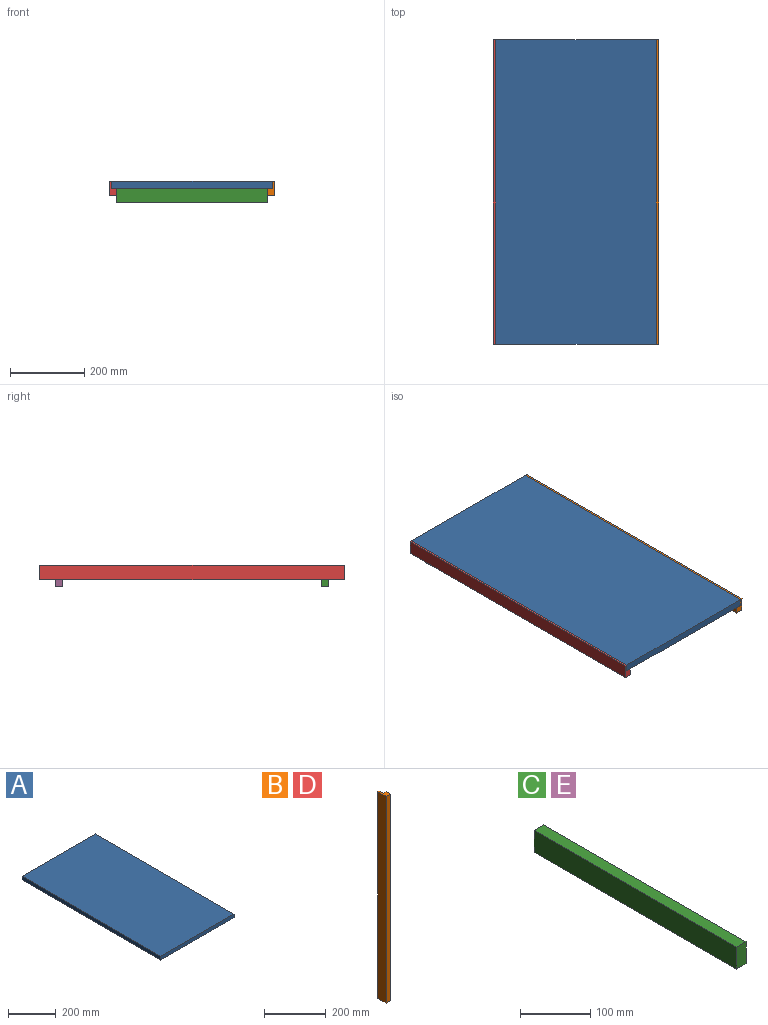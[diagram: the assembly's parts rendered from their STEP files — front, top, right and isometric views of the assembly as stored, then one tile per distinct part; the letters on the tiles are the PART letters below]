
ASSEMBLY  parts=5 mates=4
PART A: 6 faces, bbox 431.8x819.2x19.1 mm
  f0: plane 819.15x19.05mm, normal (-1,0,0), area 15604.8mm2, adj f1,f2,f3,f4
  f1: plane 819.15x431.8mm, normal (0,0,-1), area 353709mm2, adj f0,f2,f4,f5
  f2: plane 431.8x19.05mm, normal (0,1,0), area 8225.8mm2, adj f0,f1,f3,f5
  f3: plane 819.15x431.8mm, normal (0,0,1), area 353709mm2, adj f0,f2,f4,f5
  f4: plane 431.8x19.05mm, normal (0,-1,0), area 8225.8mm2, adj f0,f1,f3,f5
  f5: plane 819.15x19.05mm, normal (1,0,0), area 15604.8mm2, adj f1,f2,f3,f4
PART B: 8 faces, bbox 19.1x38.1x819.2 mm
  f0: plane 819.15x38.1mm, normal (-1,0,0), area 31209.6mm2, adj f1,f3,f4,f5
  f1: plane 819.15x19.05mm, normal (0,-1,0), area 15604.8mm2, adj f0,f2,f3,f5
  f2: plane 819.15x19.05mm, normal (1,0,0), area 15604.8mm2, adj f1,f3,f5,f6
  f3: plane 38.1x19.05mm, normal (0,0,-1), area 483.9mm2, adj f0,f1,f2,f4,f6,f7
  f4: plane 819.15x6.35mm, normal (0,1,0), area 5201.6mm2, adj f0,f3,f5,f7
  f5: plane 38.1x19.05mm, normal (0,0,1), area 483.9mm2, adj f0,f1,f2,f4,f6,f7
  f6: plane 819.15x12.7mm, normal (0,1,0), area 10403.2mm2, adj f2,f3,f5,f7
  f7: plane 819.15x19.05mm, normal (1,0,0), area 15604.8mm2, adj f3,f4,f5,f6
PART C: 6 faces, bbox 19.1x406.4x38.1 mm
  f0: plane 406.4x19.05mm, normal (0,0,1), area 7741.9mm2, adj f1,f3,f4,f5
  f1: plane 406.4x38.1mm, normal (-1,0,0), area 15483.8mm2, adj f0,f2,f4,f5
  f2: plane 406.4x19.05mm, normal (0,0,-1), area 7741.9mm2, adj f1,f3,f4,f5
  f3: plane 406.4x38.1mm, normal (1,0,0), area 15483.8mm2, adj f0,f2,f4,f5
  f4: plane 38.1x19.05mm, normal (0,-1,0), area 725.8mm2, adj f0,f1,f2,f3
  f5: plane 38.1x19.05mm, normal (0,1,0), area 725.8mm2, adj f0,f1,f2,f3
PART D: same geometry as B
PART E: same geometry as C
PLACE A t=(-316.33,212.15,-235.2)mm
PLACE B rot(axis=(0,-0.71,-0.71),180deg) t=(121.82,-607,-216.15)mm
PLACE C rot(axis=(-0.71,-0.71,0),180deg) t=(102.77,-565.72,-273.3)mm
PLACE D rot(axis=(1,0,0),90deg) t=(-322.68,212.15,-216.15)mm
PLACE E rot(axis=(0.71,-0.71,0),180deg) t=(-303.63,170.88,-273.3)mm
MATE fastened E.f2 <-> A.f1  axis (0,0,1) through (-303.63,170.88,-235.2)mm
MATE fastened C.f2 <-> A.f1  axis (0,0,1) through (-303.63,-565.72,-235.2)mm
MATE fastened B.f7 <-> A.f5  axis (-1,0,0) through (115.47,212.15,-235.2)mm
MATE fastened D.f7 <-> A.f0  axis (1,0,0) through (-316.33,-607,-235.2)mm
